# Revit family: HERZ Strömax Commissioning Valve With Test points, Straight Body 4218 GF
name_source: partatom
category: Rohrzubehör
units: mm (PartAtom-declared; Revit-internal decimal feet)

## family parameters
Arbeitsebenenbasiert = Nein
Beim Laden mit Abzugskörper schneiden = Nein
Bemaßung runder Anschluss = Durchmesser verwenden
Gemeinsam genutzt = Nein
Immer vertikal = Ja
OmniClass-Nummer = 23.65.55.14
OmniClass-Titel = Valves for Liquid Services
Teiletyp = Unterbricht

## types (1)
- HERZ Strömax Commissioning Valve With Test points, Straight Body 4218 GF
    Body = gray cast iron GJL 250 according to EN 1561
    Counting device = plastic
    Differential pressure measurement = The Strömax GF double regulating and commissioning valve is equipped with two test points:
If a suitable measuring device is used, the differential pressure can be measured and the respective flow rate can be determined depending on the setting level.
The respective flow rate can also be read directly on the HERZ measuring computers (see device manual).
When using antifreeze, the density of the medium changes, which must be taken into account when measuring differential pressure.
    Field of application = For hydraulic balancing in heating or cooling systems, regulating and shutting off distribution circuits, heat exchangers, heating and cooling terminals.
    GT = 10 mm  [stored 0.0328084 ft]
    Hersteller = HERZ Armaturen Ges.m.b.H.
    Max. operating pressure = 1600000.0 Pa
    Max. operating temperature = 110 °C
    Medium = Water purity in accordance with the ÖNORM H 5195 and VDI 2035 standards.
Ethylene and propylene glycol can be used in a ratio of 25-50 vol. [%] are mixed.
    Min. operating temperature = -10 °C
    Model = The STRÖMAX GF with test points DN 50 - 300:
Body of grey cast iron GJL 250 according to EN 1561, flange according to EN 1092, PN 16;
length according to ÖNORM EN-558-1, basic series 1; painted blue.
Thermostatic upper part of grey cast iron GJL 250.
Digital display of the pre-setting levels.
Non-rising spindle with triple O-ring seal.
    O-Ring = EPDM
    Regulation spindle = brass / stainless steel
    SCRNCODE = 05;07;02
    SCRNSEQ = ARM;ARM_TYP="STRV";2
    Spindle (from DN125) = stainless steel
    Spindle (up to DN100) = brass
    URL = www.herzvalves.com
    Upper part = gray cast iron GJL 250 according to EN 1561
    Valve cone = gray cast iron GJL 250 according to EN 1561/ EPDM coated
    Vorgabe-Ansicht = 0 mm  [stored 0 ft]
    W01 = 85.00°
    W02 = 60.00°

note: [stored X ft] marks values corroborated as IEEE doubles in the binary element streams (Revit-internal decimal feet)
